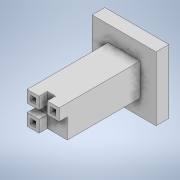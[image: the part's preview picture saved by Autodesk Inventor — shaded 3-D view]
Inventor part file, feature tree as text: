
AUTODESK INVENTOR PART (.ipt)
format: ipt  version: 2021 (Build 250183000, 183)  size: 178,688 bytes
history: native  units: in
note: dims shown in document units (in); Inventor stores cm internally (conversion verified against a paired STEP export)
features: extrude x5, sketch x5, shell x1
ambient origin geometry x8: Origin, YZ Plane, XZ Plane, XY Plane, X Axis, Y Axis, Z Axis, Center Point
bodies: Solid1 (feature_tree)
feature tree (11):
  extrude  "Extrusion1"  Depth=3.937in
  extrude  "Extrusion2"  Depth=0.7874in TaperAngle=0.0deg
  shell  "Shell1"  Thickness=0.9843in
  extrude  "Extrusion3"  Depth=0.9843in
  extrude  "Extrusion4"  Depth=3.937in TaperAngle=0.0deg
  extrude  "Extrusion5"  Depth=0.5374in TaperAngle=0.0deg
  sketch  "Sketch1"  dims[d0=3.937in d1=3.937in]
  sketch  "Sketch2"  dims[d2=3.937in d3=0.7874in d4=0.0in d5=0.9843in]
  sketch  "Sketch3"  dims[d6=0.9843in d7=0.9843in]
  sketch  "Sketch4"  dims[d8=0.9843in d9=3.937in d10=0.0in]
  sketch  "Sketch5"  dims[d11=0.3937in d12=0.5374in d13=0.0in d14=0.7339in d15=0.7339in d16=0.7339in d17=0.7339in d18=0.7339in d19=0.5039in d20=0.0in d21=0.1969in d22=0.1969in d23=0.1969in d24=0.1969in d25=0.1969in d26=0.1969in d27=0.1969in d28=0.1969in d29=0.1969in d30=0.5906in d31=0.0in]
